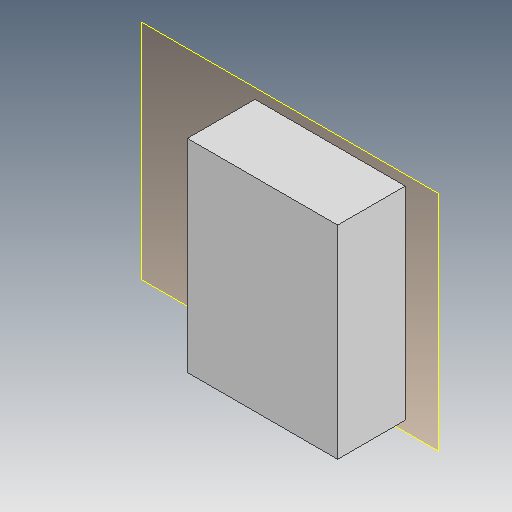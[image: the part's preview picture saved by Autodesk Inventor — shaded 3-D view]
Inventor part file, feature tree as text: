
AUTODESK INVENTOR PART (.ipt)
format: ipt  version: 2020 (Build 240168000, 168)  size: 88,064 bytes
history: native  units: mm
features: other x5, extrude x1, sketch x1
ambient origin geometry x8: Origin, YZ Plane, XZ Plane, XY Plane, X Axis, Y Axis, Z Axis, Center Point
bodies: Body1 (feature_tree)
feature tree (7):
  other  "Sólido1"
  other  "Plano de trabalho1"
  extrude  "Extrusão1"  [1 undecoded]
  sketch  "Esboço1"  dims[d0=50.0mm d1=0.0mm]
  other  "Referência1"
  other  "Montagem1"
  other  "Base:2"
note: 1 required parameter value undecoded (feature->parameter linkage not recoverable at this tier; creation-order binding heuristic only, values carry confidence <= 0.55)
